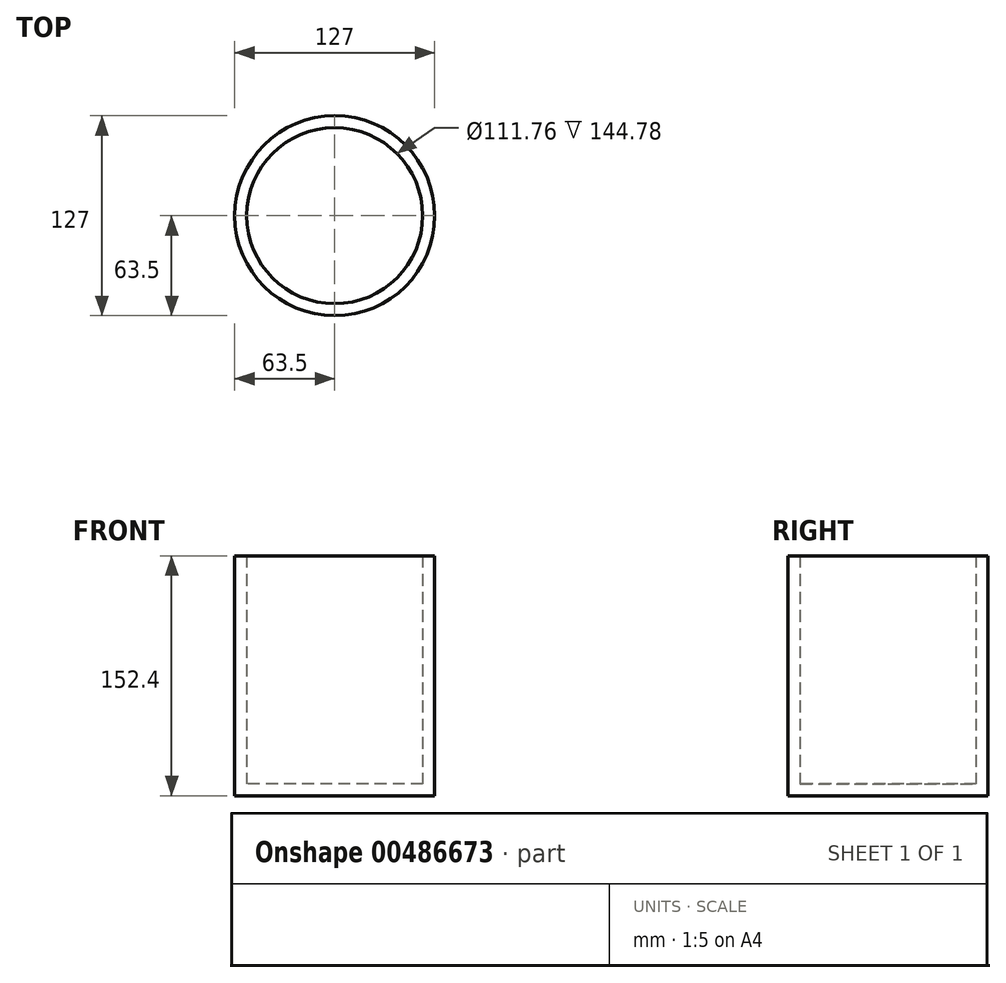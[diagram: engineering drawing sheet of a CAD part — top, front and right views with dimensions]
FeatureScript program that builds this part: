
annotation { "Feature Type Name" : "Feature", "Feature Type Description" : "" }
export const myFeature = defineFeature(function(context is Context, id is Id, definition is map)
    precondition{}
    {
        {
            var Q0;
            Q0=qCreatedBy(makeId("Top.planeOp"),FACE);
            var sketch = newSketch(context, id + "F0", { "sketchPlane" : qUnion([Q0])});
            skCircle(sketch, "E0", {"center": v(-8.57, 9.54) * mm, "radius": 63.5 * mm});
            skSolve(sketch);
        }
        {
            var Q0;
            Q0=makeQuery(id+"F0.imprint","IMPRINT",FACE,{"disambiguationData":[TD([[makeQuery(id+"F0.imprint","IMPRINT",EDGE,{"derivedFrom":sQuery(id+"F0.wireOp",EDGE,"E0")}),1.0]])]});
            extrude(context, id + "F1", {"entities" : qUnion([Q0]), "depth" : 152.4 * mm});
        }
        {
            var Q0;
            Q0=makeQuery(id+"F1.opExtrude","SWEPT_BODY",BODY,{"disambiguationData":[OSD([sQuery(id+"F0.wireOp",EDGE,"E0")])]});
            transform(context, id + "F2", {"entities" : qUnion([Q0]), "transformType" : TransformType.TRANSLATION_3D, "dx" : 8.57 * mm, "dy" : -9.54 * mm, "dz" : 0 * mm, "makeCopy" : false});
        }
        {
            var Q0;
            Q0=makeQuery(id+"F1.opExtrude","CAP_FACE",FACE,{"disambiguationData":[OSD([sQuery(id+"F0.wireOp",EDGE,"E0")])],"isStart":false});
            shell(context, id + "F3", {"entities" : qUnion([Q0]), "thickness" : 7.62 * mm});
        }
    });
